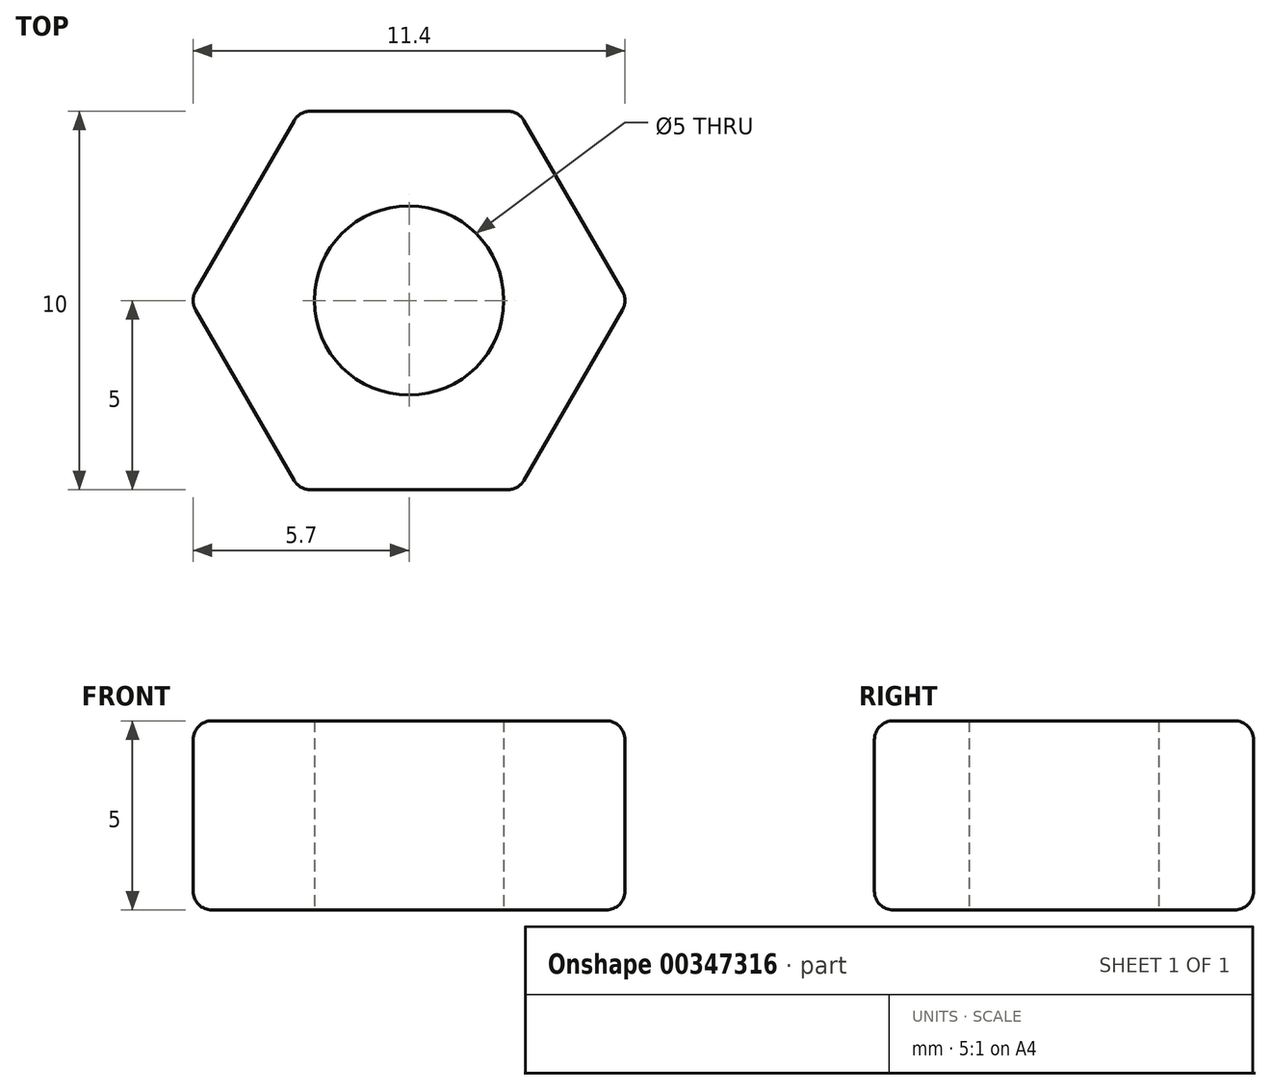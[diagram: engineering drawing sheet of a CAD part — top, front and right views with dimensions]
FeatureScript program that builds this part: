
annotation { "Feature Type Name" : "Feature", "Feature Type Description" : "" }
export const myFeature = defineFeature(function(context is Context, id is Id, definition is map)
    precondition{}
    {
        {
            var Q0;
            Q0=qCreatedBy(makeId("Top.planeOp"),FACE);
            var sketch = newSketch(context, id + "F0", { "sketchPlane" : qUnion([Q0])});
            skCircle(sketch, "E0.cCircle", {"center": v(0, 0) * mm, "radius": 5 * mm, "construction": true});
            skLineSegment(sketch, "E0.0", {"start": v(2.89, 5) * mm, "end": v(5.77, 0) * mm});
            skLineSegment(sketch, "E0.1", {"start": v(5.77, 0) * mm, "end": v(2.89, -5) * mm});
            skLineSegment(sketch, "E0.2", {"start": v(2.89, -5) * mm, "end": v(-2.89, -5) * mm});
            skLineSegment(sketch, "E0.3", {"start": v(-2.89, -5) * mm, "end": v(-5.77, 0) * mm});
            skLineSegment(sketch, "E0.4", {"start": v(-5.77, 0) * mm, "end": v(-2.89, 5) * mm});
            skLineSegment(sketch, "E0.5", {"start": v(-2.89, 5) * mm, "end": v(2.89, 5) * mm});
            skPoint(sketch, "E0.0.midPoint", {"position": v(4.33, 2.5) * mm});
            skCircle(sketch, "E1", {"center": v(0, 0) * mm, "radius": 2.5 * mm});
            skSolve(sketch);
        }
        {
            var Q0;
            Q0 = qSketchRegion(id + "F0", true);
            extrude(context, id + "F1", {"entities" : qUnion([Q0]), "depth" : 5 * mm});
        }
        {
            var Q0;
            Q0=makeQuery(id+"F1.opExtrude","CAP_EDGE",EDGE,{"disambiguationData":[OSD([sQuery(id+"F0.wireOp",EDGE,"E0.4")])],"isStart":true});
            var Q1;
            Q1=makeQuery(id+"F1.opExtrude","CAP_EDGE",EDGE,{"disambiguationData":[OSD([sQuery(id+"F0.wireOp",EDGE,"E0.3")])],"isStart":true});
            var Q2;
            Q2=makeQuery(id+"F1.opExtrude","SWEPT_FACE",FACE,{"disambiguationData":[OSD([sQuery(id+"F0.wireOp",EDGE,"E0.2")])]});
            var Q3;
            Q3=makeQuery(id+"F1.opExtrude","SWEPT_FACE",FACE,{"disambiguationData":[OSD([sQuery(id+"F0.wireOp",EDGE,"E0.3")])]});
            var Q4;
            Q4=makeQuery(id+"F1.opExtrude","SWEPT_FACE",FACE,{"disambiguationData":[OSD([sQuery(id+"F0.wireOp",EDGE,"E0.4")])]});
            var Q5;
            Q5=makeQuery(id+"F1.opExtrude","SWEPT_FACE",FACE,{"disambiguationData":[OSD([sQuery(id+"F0.wireOp",EDGE,"E0.0")])]});
            var Q6;
            Q6=makeQuery(id+"F1.opExtrude","SWEPT_FACE",FACE,{"disambiguationData":[OSD([sQuery(id+"F0.wireOp",EDGE,"E0.5")])]});
            var Q7;
            Q7=makeQuery(id+"F1.opExtrude","SWEPT_FACE",FACE,{"disambiguationData":[OSD([sQuery(id+"F0.wireOp",EDGE,"E0.1")])]});
            fillet(context, id + "F2", {"entities" : qUnion([Q0, Q1, Q2, Q3, Q4, Q5, Q6, Q7]), "radius" : 0.5 * mm, "tangentPropagation" : true, "allowEdgeOverflow" : false});
        }
    });
